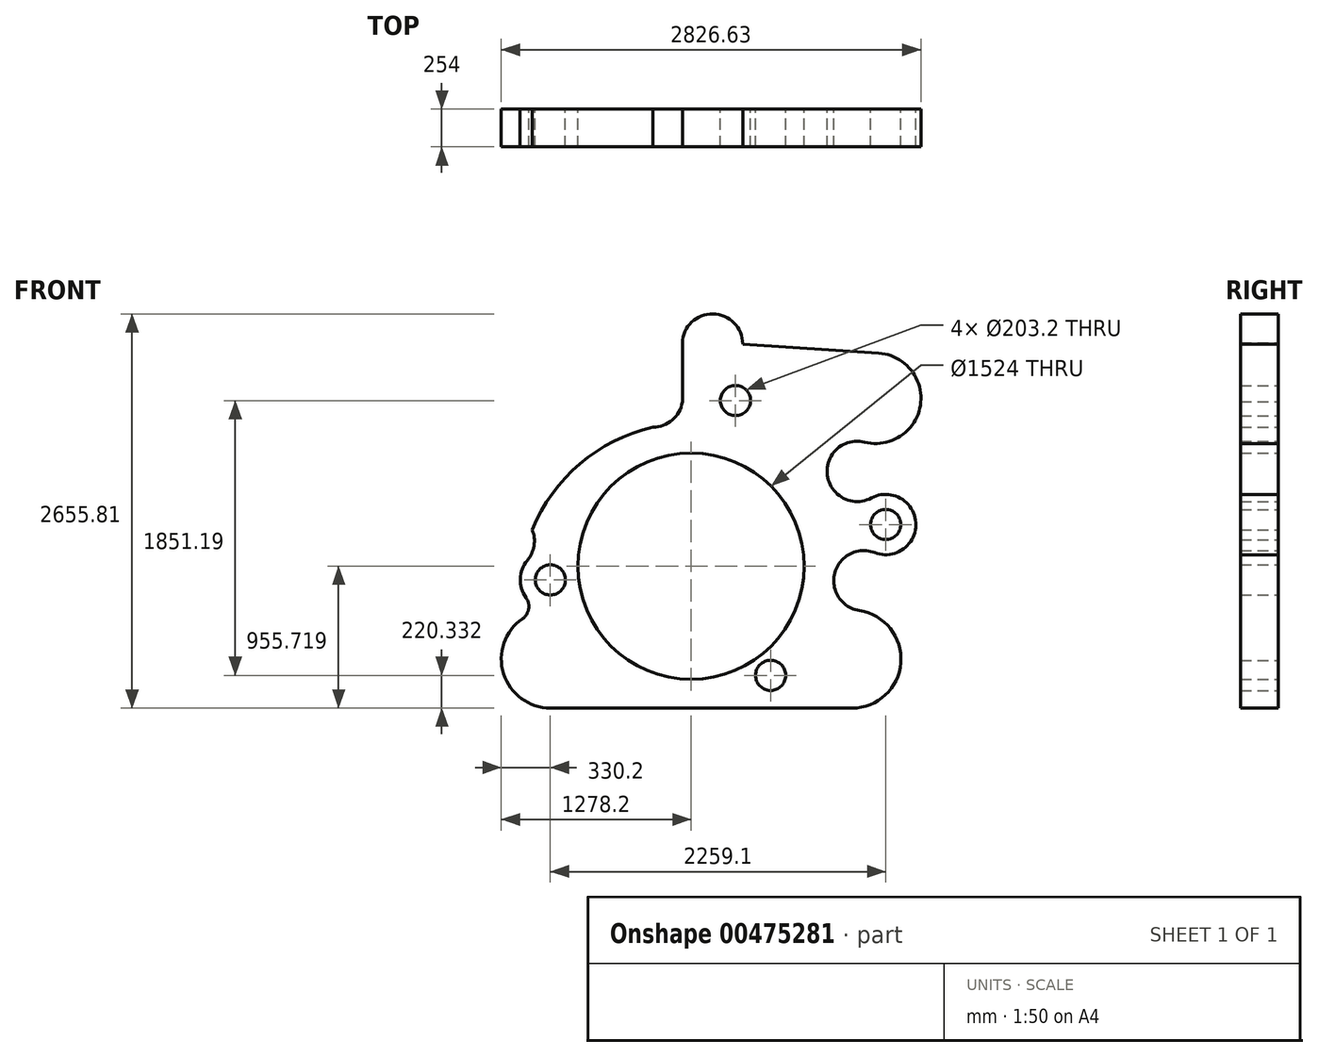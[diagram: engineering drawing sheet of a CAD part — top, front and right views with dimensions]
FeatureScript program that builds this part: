
annotation { "Feature Type Name" : "Feature", "Feature Type Description" : "" }
export const myFeature = defineFeature(function(context is Context, id is Id, definition is map)
    precondition{}
    {
        {
            var Q0;
            Q0=qCreatedBy(makeId("Front.planeOp"),FACE);
            var sketch = newSketch(context, id + "F0", { "sketchPlane" : qUnion([Q0])});
            skArc(sketch, "E0", {"start": v(-188.65, 271) * mm, "mid": v(-315.05, -98.86) * mm, "end": v(0, -330.2) * mm});
            skArc(sketch, "E1", {"start": v(-188.65, 271) * mm, "mid": v(-146.52, 337.45) * mm, "end": v(-164.46, 414.06) * mm});
            skArc(sketch, "E2", {"start": v(-155.4, 664.31) * mm, "mid": v(-203.07, 540.75) * mm, "end": v(-164.46, 414.06) * mm});
            skArc(sketch, "E3", {"start": v(-155.4, 664.31) * mm, "mid": v(-110.14, 763.32) * mm, "end": v(-122.47, 871.49) * mm});
            skLineSegment(sketch, "E4", {"start": v(0, -330.2) * mm, "end": v(2032, -330.2) * mm});
            skArc(sketch, "E5", {"start": v(2032, -330.2) * mm, "mid": v(2361.26, -24.91) * mm, "end": v(2081.69, 326.44) * mm});
            skArc(sketch, "E6", {"start": v(2185.68, 716.8) * mm, "mid": v(1915.91, 579.64) * mm, "end": v(2081.69, 326.44) * mm});
            skArc(sketch, "E7", {"start": v(2185.68, 716.8) * mm, "mid": v(2461.92, 918.66) * mm, "end": v(2163.16, 1085.4) * mm});
            skArc(sketch, "E8", {"start": v(2116.99, 1461.54) * mm, "mid": v(1865.54, 1239.77) * mm, "end": v(2163.16, 1085.4) * mm});
            skArc(sketch, "E9", {"start": v(2116.99, 1461.54) * mm, "mid": v(2492.68, 1709.38) * mm, "end": v(2211.95, 2061.18) * mm});
            skLineSegment(sketch, "E10", {"start": v(2211.95, 2061.18) * mm, "end": v(1295.56, 2122.41) * mm});
            skArc(sketch, "E11", {"start": v(1295.56, 2122.41) * mm, "mid": v(1088.77, 2325.58) * mm, "end": v(889.29, 2115.22) * mm});
            skArc(sketch, "E12", {"start": v(689.92, 1561.55) * mm, "mid": v(820.9, 1610.45) * mm, "end": v(889.29, 1732.4) * mm});
            skLineSegment(sketch, "E13", {"start": v(889.29, 2129.6) * mm, "end": v(889.29, 1732.4) * mm});
            skArc(sketch, "E14", {"start": v(689.92, 1561.55) * mm, "mid": v(199.47, 1315.72) * mm, "end": v(-122.47, 871.49) * mm});
            skCircle(sketch, "E15", {"center": v(948, 625.52) * mm, "radius": 762 * mm});
            skCircle(sketch, "E16", {"center": v(1246.98, 1741.33) * mm, "radius": 101.6 * mm});
            skCircle(sketch, "E17", {"center": v(2259.1, 906.27) * mm, "radius": 101.6 * mm});
            skCircle(sketch, "E18", {"center": v(1484.07, -109.87) * mm, "radius": 101.6 * mm});
            skCircle(sketch, "E19", {"center": v(0, 533.4) * mm, "radius": 101.6 * mm});
            skSolve(sketch);
        }
        {
            var Q0;
            Q0=makeQuery(id+"F0.imprint","IMPRINT",FACE,{"disambiguationData":[TD([[makeQuery(id+"F0.imprint","IMPRINT",EDGE,{"derivedFrom":sQuery(id+"F0.wireOp",EDGE,"E0")}),1.0]])]});
            extrude(context, id + "F1", {"entities" : qUnion([Q0]), "depth" : 254 * mm});
        }
    });
